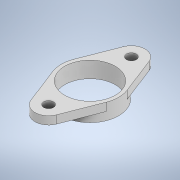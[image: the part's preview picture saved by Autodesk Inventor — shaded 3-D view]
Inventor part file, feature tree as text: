
AUTODESK INVENTOR PART (.ipt)
format: ipt  version: 2021 (Build 250183000, 183)  size: 132,608 bytes
history: native  units: mm
features: extrude x2, sketch x2
ambient origin geometry x8: Origin, YZ Plane, XZ Plane, XY Plane, X Axis, Y Axis, Z Axis, Center Point
bodies: Solid1 (feature_tree)
feature tree (4):
  extrude  "Extrusion1"  Depth=25.0mm
  extrude  "Extrusion2"  Depth=3.5mm
  sketch  "Sketch1"  dims[d0=22.0mm d1=25.0mm]
  sketch  "Sketch2"  dims[d2=7.0mm d3=0.0mm d4=4.3mm d5=4.3mm d6=0.0mm d7=0.0mm d8=18.05mm d9=18.05mm d10=3.8mm d11=3.8mm d12=3.5mm d13=0.0mm]
